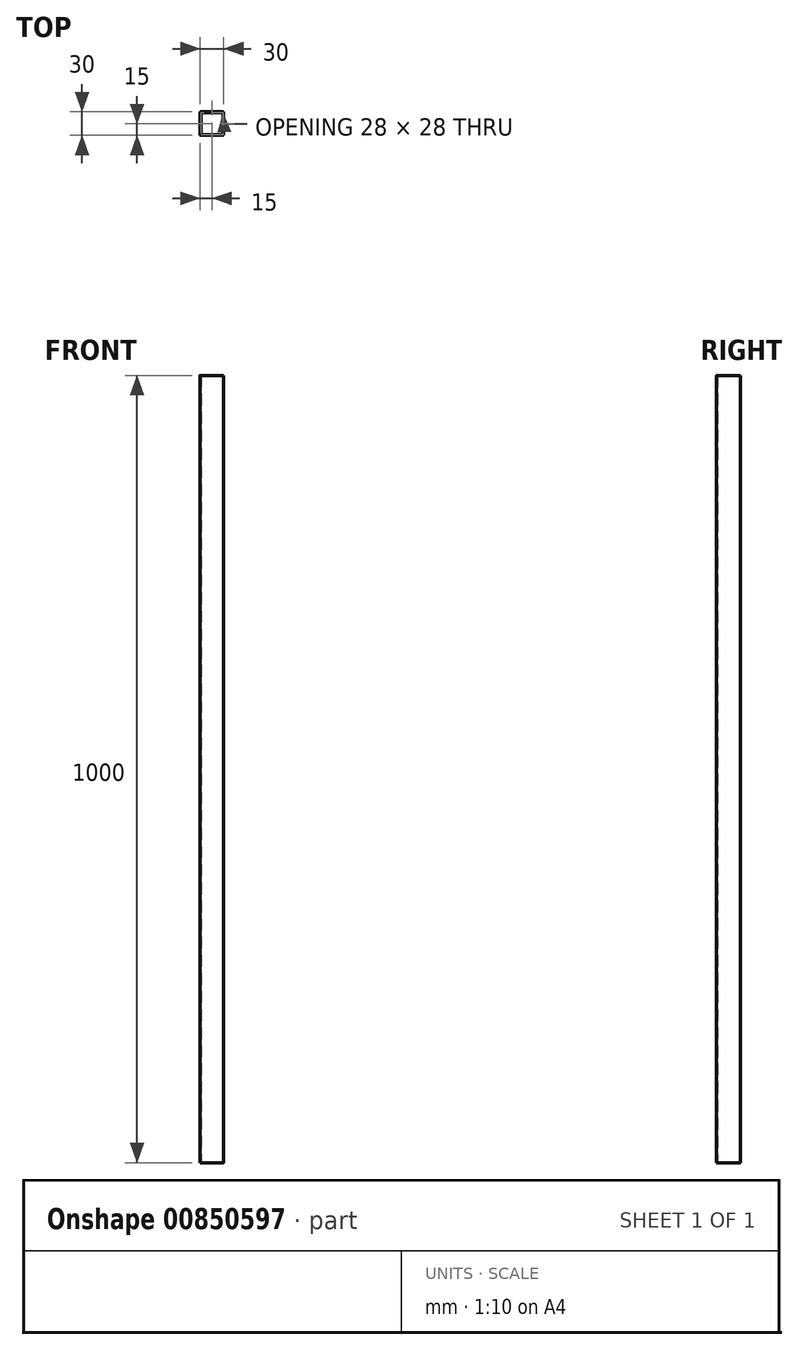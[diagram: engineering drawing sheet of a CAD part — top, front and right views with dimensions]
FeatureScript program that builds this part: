
annotation { "Feature Type Name" : "Feature", "Feature Type Description" : "" }
export const myFeature = defineFeature(function(context is Context, id is Id, definition is map)
    precondition{}
    {
        {
            var Q0;
            Q0=qCreatedBy(makeId("Top.planeOp"),FACE);
            var sketch = newSketch(context, id + "F0", { "sketchPlane" : qUnion([Q0])});
            skLineSegment(sketch, "E0.bottom", {"start": v(-15, 15) * mm, "end": v(15, 15) * mm});
            skLineSegment(sketch, "E0.top", {"start": v(-15, -15) * mm, "end": v(15, -15) * mm});
            skLineSegment(sketch, "E0.left", {"start": v(-15, 15) * mm, "end": v(-15, -15) * mm});
            skLineSegment(sketch, "E0.right", {"start": v(15, 15) * mm, "end": v(15, -15) * mm});
            skLineSegment(sketch, "E1.bottom", {"start": v(-14, 14) * mm, "end": v(14, 14) * mm});
            skLineSegment(sketch, "E1.top", {"start": v(-14, -14) * mm, "end": v(14, -14) * mm});
            skLineSegment(sketch, "E1.left", {"start": v(-14, 14) * mm, "end": v(-14, -14) * mm});
            skLineSegment(sketch, "E1.right", {"start": v(14, 14) * mm, "end": v(14, -14) * mm});
            skSolve(sketch);
        }
        {
            var Q0;
            Q0 = qSketchRegion(id + "F0", true);
            extrude(context, id + "F1", {"entities" : qUnion([Q0]), "endBound" : BoundingType.SYMMETRIC, "depth" : 1000 * mm, "offsetDistance" : 25 * mm});
        }
        {
            var Q0;
            Q0=makeQuery(id+"F1.opExtrude","SWEPT_EDGE",EDGE,{"disambiguationData":[OSD([sQuery(id+"F0.wireOp",EDGE,"E1.bottom"),sQuery(id+"F0.wireOp",EDGE,"E1.right")])]});
            var Q1;
            Q1=makeQuery(id+"F1.opExtrude","SWEPT_EDGE",EDGE,{"disambiguationData":[OSD([sQuery(id+"F0.wireOp",EDGE,"E1.bottom"),sQuery(id+"F0.wireOp",EDGE,"E1.left")])]});
            var Q2;
            Q2=makeQuery(id+"F1.opExtrude","SWEPT_EDGE",EDGE,{"disambiguationData":[OSD([sQuery(id+"F0.wireOp",EDGE,"E1.top"),sQuery(id+"F0.wireOp",EDGE,"E1.left")])]});
            var Q3;
            Q3=makeQuery(id+"F1.opExtrude","SWEPT_EDGE",EDGE,{"disambiguationData":[OSD([sQuery(id+"F0.wireOp",EDGE,"E1.top"),sQuery(id+"F0.wireOp",EDGE,"E1.right")])]});
            var Q4;
            Q4=makeQuery(id+"F1.opExtrude","SWEPT_EDGE",EDGE,{"disambiguationData":[OSD([sQuery(id+"F0.wireOp",EDGE,"E0.bottom"),sQuery(id+"F0.wireOp",EDGE,"E0.left")])]});
            var Q5;
            Q5=makeQuery(id+"F1.opExtrude","SWEPT_EDGE",EDGE,{"disambiguationData":[OSD([sQuery(id+"F0.wireOp",EDGE,"E0.top"),sQuery(id+"F0.wireOp",EDGE,"E0.left")])]});
            var Q6;
            Q6=makeQuery(id+"F1.opExtrude","SWEPT_EDGE",EDGE,{"disambiguationData":[OSD([sQuery(id+"F0.wireOp",EDGE,"E0.bottom"),sQuery(id+"F0.wireOp",EDGE,"E0.right")])]});
            var Q7;
            Q7=makeQuery(id+"F1.opExtrude","SWEPT_EDGE",EDGE,{"disambiguationData":[OSD([sQuery(id+"F0.wireOp",EDGE,"E0.top"),sQuery(id+"F0.wireOp",EDGE,"E0.right")])]});
            fillet(context, id + "F2", {"entities" : qUnion([Q0, Q1, Q2, Q3, Q4, Q5, Q6, Q7]), "radius" : 1.5 * mm, "tangentPropagation" : true, "allowEdgeOverflow" : false});
        }
    });
